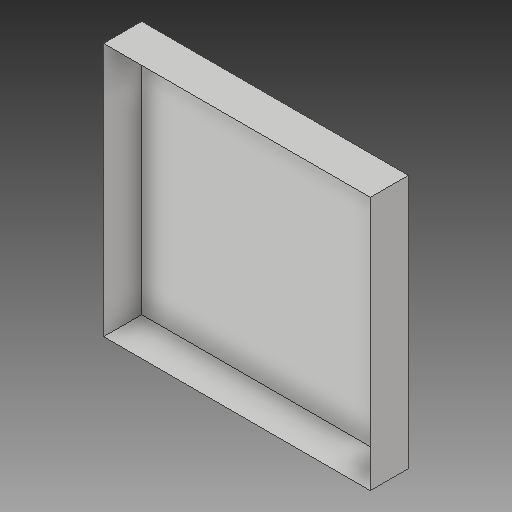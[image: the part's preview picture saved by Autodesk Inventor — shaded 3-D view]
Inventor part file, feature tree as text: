
AUTODESK INVENTOR PART (.ipt)
format: ipt  version: 2017 (Build 210142000, 142)  size: 95,744 bytes
history: native  units: in
note: dims shown in document units (in); Inventor stores cm internally (conversion verified against a paired STEP export)
features: other x2, sketch x1
ambient origin geometry x8: Origin, YZ Plane, XZ Plane, XY Plane, X Axis, Y Axis, Z Axis, Center Point
bodies: Solid1 (feature_tree)
feature tree (3):
  other  "end cap"
  other  "removed end"
  sketch  "Sketch1"  dims[d0=7.0in d1=6.6667in d2=1.0in d3=0.0in]
